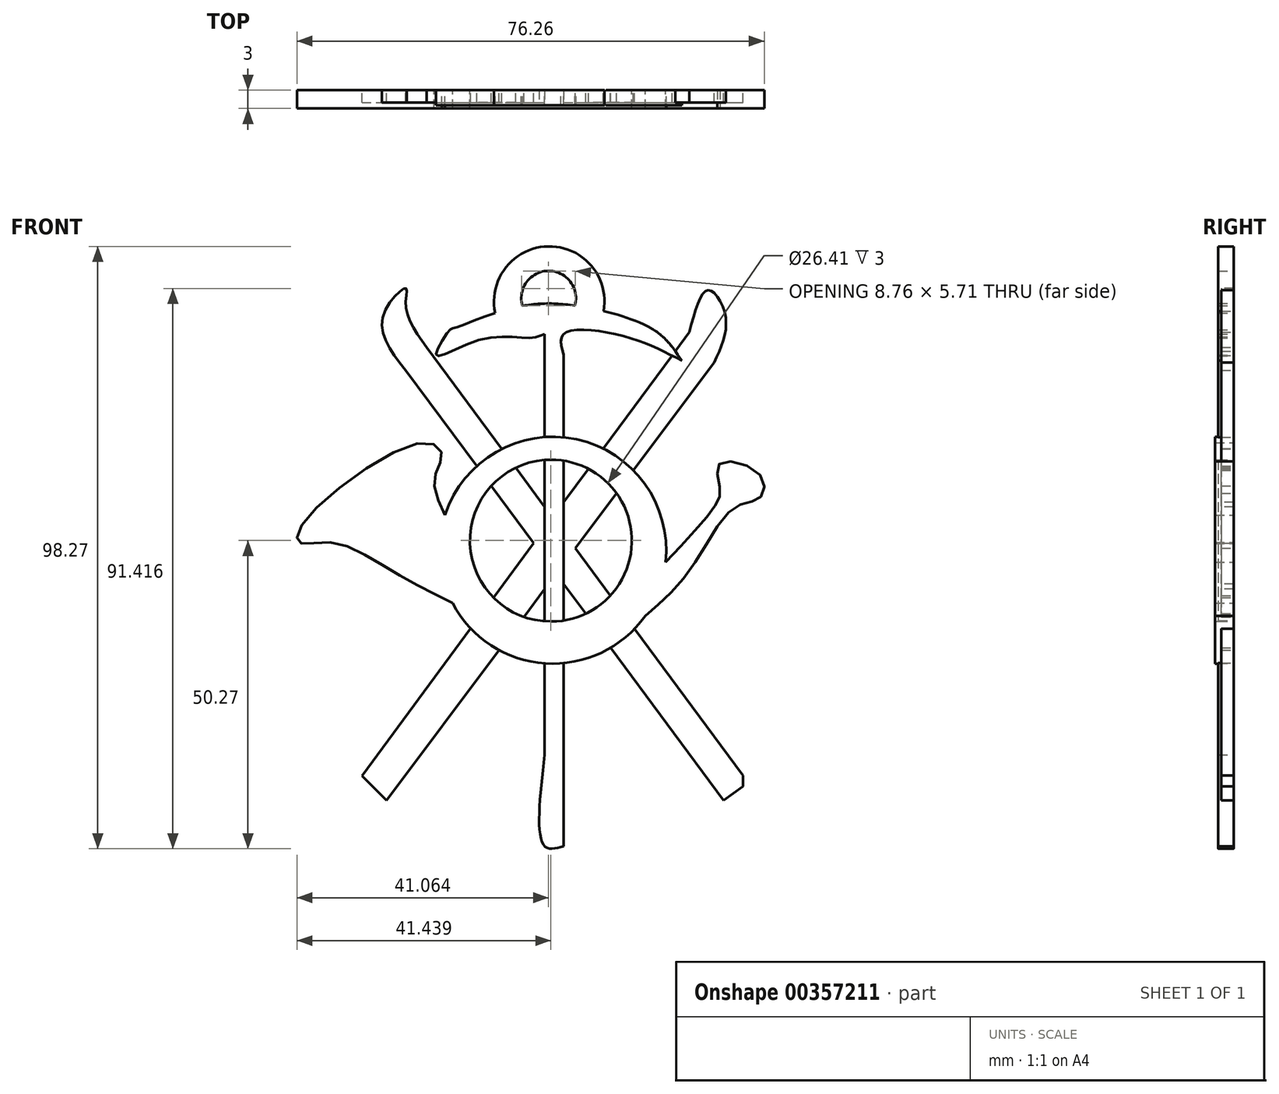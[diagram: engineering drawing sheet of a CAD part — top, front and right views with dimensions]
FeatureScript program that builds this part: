
annotation { "Feature Type Name" : "Feature", "Feature Type Description" : "" }
export const myFeature = defineFeature(function(context is Context, id is Id, definition is map)
    precondition{}
    {
        {
            var Q0;
            Q0=qCreatedBy(makeId("Front.planeOp"),FACE);
            var sketch = newSketch(context, id + "F0", { "sketchPlane" : qUnion([Q0])});
            skLineSegment(sketch, "E0", {"start": v(-5.9, -42.1) * mm, "end": v(-2.76, -39.77) * mm});
            skFitSpline(sketch, "E1", {"points": [v(-57.78, 28.11) * mm, v(-61.5, 36.81) * mm, v(-57.78, 41.47) * mm, v(-57.78, 38.68) * mm, v(-54.36, 31.84) * mm], "startDerivative": vector(-21.83, 27.74) * mm, "endDerivative": vector(17.8, -24.83) * mm});
            skLineSegment(sketch, "E2", {"start": v(-64.93, -38.05) * mm, "end": v(-60.89, -42.1) * mm});
            skLineSegment(sketch, "E3", {"start": v(-60.89, -42.1) * mm, "end": v(-7.46, 29.36) * mm});
            skLineSegment(sketch, "E4", {"start": v(-64.93, -38.05) * mm, "end": v(-11.5, 34.33) * mm});
            skFitSpline(sketch, "E5", {"points": [v(-11.5, 34.33) * mm, v(-8.39, 41.16) * mm, v(-5.6, 36.81) * mm, v(-7.46, 29.36) * mm], "startDerivative": vector(7.65, 28.9) * mm, "endDerivative": vector(-9.57, -20.44) * mm});
            skLineSegment(sketch, "E6", {"start": v(-57.78, 28.11) * mm, "end": v(-5.9, -42.1) * mm});
            skLineSegment(sketch, "E7", {"start": v(-54.36, 31.84) * mm, "end": v(-2.76, -38) * mm});
            skLineSegment(sketch, "E8", {"start": v(-2.76, -39.77) * mm, "end": v(-2.76, -38) * mm});
            skSolve(sketch);
        }
        {
            var Q0;
            Q0=qCreatedBy(makeId("Front.planeOp"),FACE);
            var sketch = newSketch(context, id + "F1", { "sketchPlane" : qUnion([Q0])});
            skFitSpline(sketch, "E9", {"points": [v(-12.74, 29.67) * mm, v(-16.78, 34.33) * mm, v(-25.47, 37.74) * mm, v(-34.8, 38.99) * mm, v(-43.18, 37.43) * mm, v(-50.01, 34.95) * mm, v(-50.64, 34.64) * mm, v(-52.81, 30.6) * mm, v(-45.67, 33.08) * mm, v(-37.28, 33.4) * mm, v(-35.1, 34.02) * mm], "startDerivative": vector(-32.85, 49.36) * mm, "endDerivative": vector(29.67, 13.78) * mm});
            skLineSegment(sketch, "E10", {"start": v(-35.1, 34.02) * mm, "end": v(-35.1, -34.64) * mm});
            skLineSegment(sketch, "E11", {"start": v(-32, 30.6) * mm, "end": v(-32, -36.2) * mm});
            skFitSpline(sketch, "E12", {"points": [v(-32, -36.2) * mm, v(-32, -49.55) * mm], "startDerivative": vector(0, -13.36) * mm, "endDerivative": vector(0, -13.36) * mm});
            skFitSpline(sketch, "E13", {"points": [v(-32, -49.55) * mm, v(-35.1, -49.55) * mm, v(-35.1, -34.64) * mm], "startDerivative": vector(-11.47, -3.4) * mm, "endDerivative": vector(3.4, 29.17) * mm});
            skFitSpline(sketch, "E14", {"points": [v(-32, 30.6) * mm, v(-32, 34.02) * mm, v(-22.37, 33.7) * mm, v(-12.74, 29.67) * mm], "startDerivative": vector(-5.18, 17.89) * mm, "endDerivative": vector(21.91, -11.45) * mm});
            skArc(sketch, "E15", {"start": v(-30.17, 38.66) * mm, "mid": v(-34.49, 44.3) * mm, "end": v(-38.74, 38.6) * mm});
            skArc(sketch, "E16", {"start": v(-25.47, 37.74) * mm, "mid": v(-34.52, 48.31) * mm, "end": v(-43.18, 37.43) * mm});
            skSolve(sketch);
        }
        {
            var Q0;
            Q0=qCreatedBy(makeId("Front.planeOp"),FACE);
            var sketch = newSketch(context, id + "F2", { "sketchPlane" : qUnion([Q0])});
            skCircle(sketch, "E17", {"center": v(-33.78, -1.26) * mm, "radius": 18.5 * mm});
            skPoint(sketch, "E17.first.point", {"position": v(-34.17, 17.24) * mm});
            skPoint(sketch, "E17.second.point", {"position": v(-32.62, -19.73) * mm});
            skPoint(sketch, "E17.third.point", {"position": v(-21.12, -14.76) * mm});
            skCircle(sketch, "E18", {"center": v(-34.1, 0.3) * mm, "radius": 13.2 * mm});
            skPoint(sketch, "E18.first.point", {"position": v(-33.86, 13.51) * mm});
            skPoint(sketch, "E18.second.point", {"position": v(-33.78, -12.9) * mm});
            skPoint(sketch, "E18.third.point", {"position": v(-22.06, -5.13) * mm});
            skFitSpline(sketch, "E19", {"points": [v(-51.37, 4.48) * mm, v(-53.12, 10.4) * mm, v(-51.88, 14.13) * mm, v(-54.67, 16.3) * mm, v(-73.93, 3.88) * mm, v(-75.18, 0) * mm, v(-69.9, 0) * mm, v(-60.27, -4.5) * mm, v(-50.14, -9.9) * mm], "startDerivative": vector(-26.52, 55.76) * mm, "endDerivative": vector(65.93, -33.26) * mm});
            skFitSpline(sketch, "E20", {"points": [v(-15.38, -3.24) * mm, v(-7.46, 5.75) * mm, v(-6.52, 8.85) * mm, v(-6.52, 12.9) * mm, v(0, 11.03) * mm, v(0, 7.3) * mm, v(-4.04, 5.75) * mm, v(-11.18, -4.2) * mm, v(-18.71, -12) * mm], "startDerivative": vector(57.58, 61.38) * mm, "endDerivative": vector(-49.06, -41.96) * mm});
            skSolve(sketch);
        }
        {
            var Q0;
            Q0 = qSketchRegion(id + "F2", true);
            extrude(context, id + "F3", {"entities" : qUnion([Q0]), "depth" : 3 * mm});
        }
        {
            var Q0;
            Q0 = qSketchRegion(id + "F1", true);
            extrude(context, id + "F4", {"entities" : qUnion([Q0]), "operationType" : NewBodyOperationType.ADD, "depth" : 2.5 * mm});
        }
        {
            var Q0;
            Q0 = qSketchRegion(id + "F0", true);
            extrude(context, id + "F5", {"entities" : qUnion([Q0]), "operationType" : NewBodyOperationType.ADD, "depth" : 2 * mm});
        }
    });
